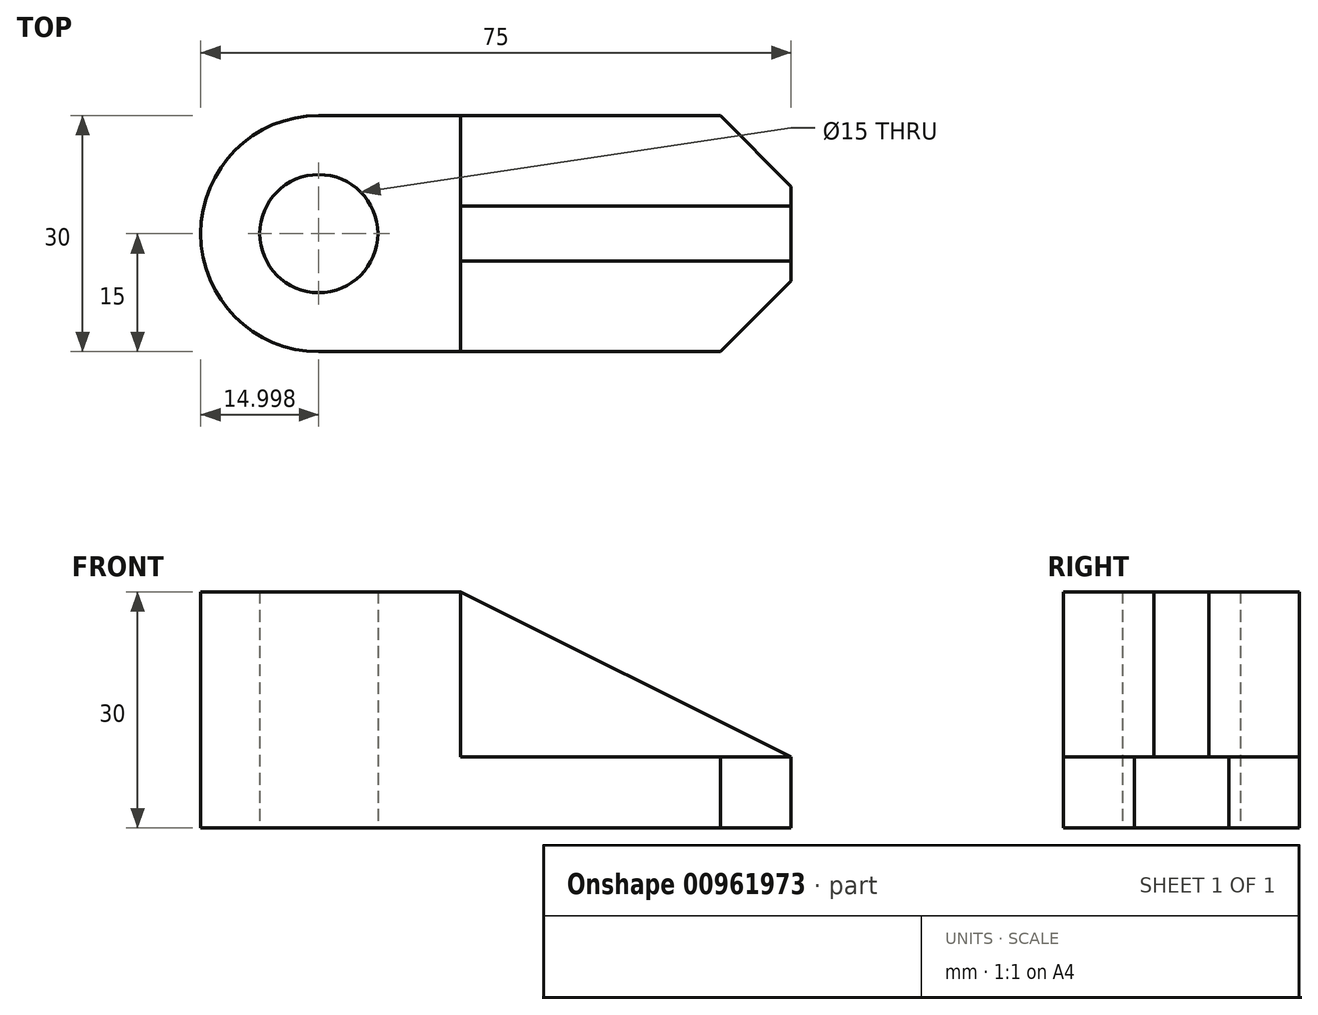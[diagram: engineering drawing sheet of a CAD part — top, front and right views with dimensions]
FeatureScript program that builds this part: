
annotation { "Feature Type Name" : "Feature", "Feature Type Description" : "" }
export const myFeature = defineFeature(function(context is Context, id is Id, definition is map)
    precondition{}
    {
        {
            var Q0;
            Q0=qCreatedBy(makeId("Top.planeOp"),FACE);
            var sketch = newSketch(context, id + "F0", { "sketchPlane" : qUnion([Q0])});
            skCircle(sketch, "E0", {"center": v(-60.56, 0) * mm, "radius": 7.5 * mm});
            skArc(sketch, "E1", {"start": v(-60.56, 15) * mm, "mid": v(-75.56, 0) * mm, "end": v(-60.56, -15) * mm});
            skLineSegment(sketch, "E2.bottom", {"start": v(-60.56, -15) * mm, "end": v(-0.56, -15) * mm});
            skLineSegment(sketch, "E2.top", {"start": v(-60.56, 15) * mm, "end": v(-0.56, 15) * mm});
            skLineSegment(sketch, "E2.right", {"start": v(-0.56, -15) * mm, "end": v(-0.56, 15) * mm});
            skLineSegment(sketch, "E3", {"start": v(-42.56, 15) * mm, "end": v(-42.56, -15) * mm});
            skSolve(sketch);
        }
        {
            var Q0;
            Q0=makeQuery(id+"F0.imprint","IMPRINT",FACE,{"disambiguationData":[TD([[makeQuery(id+"F0.imprint","IMPRINT",EDGE,{"derivedFrom":sQuery(id+"F0.wireOp",EDGE,"E0")}),-1.0]])]});
            extrude(context, id + "F1", {"entities" : qUnion([Q0]), "depth" : 30 * mm, "offsetDistance" : 25 * mm});
        }
        {
            var Q0;
            {var subQ0=sQuery(id+"F0.wireOp",EDGE,"E2.right");Q0=makeQuery(id+"F0.imprint","IMPRINT",FACE,{"disambiguationData":[TD([[makeQuery(id+"F0.imprint","IMPRINT",EDGE,{"derivedFrom":subQ0}),1.0]])]});}
            extrude(context, id + "F2", {"entities" : qUnion([Q0]), "operationType" : NewBodyOperationType.ADD, "depth" : 9 * mm, "offsetDistance" : 25 * mm});
        }
        {
            var Q0;
            Q0=makeQuery(id+"F2.opExtrude","SWEPT_EDGE",EDGE,{"disambiguationData":[OSD([sQuery(id+"F0.wireOp",EDGE,"E2.bottom"),sQuery(id+"F0.wireOp",EDGE,"E2.right")])]});
            var Q1;
            Q1=makeQuery(id+"F2.opExtrude","SWEPT_EDGE",EDGE,{"disambiguationData":[OSD([sQuery(id+"F0.wireOp",EDGE,"E2.top"),sQuery(id+"F0.wireOp",EDGE,"E2.right")])]});
            chamfer(context, id + "F3", {"entities" : qUnion([Q0, Q1]), "width" : 9 * mm, "tangentPropagation" : true});
        }
        {
            var Q0;
            Q0=qCreatedBy(makeId("Front.planeOp"),FACE);
            var sketch = newSketch(context, id + "F4", { "sketchPlane" : qUnion([Q0])});
            skPoint(sketch, "E4.0", {"position": v(-0.56, 9) * mm});
            skPoint(sketch, "E5.0", {"position": v(-42.56, 30) * mm});
            skLineSegment(sketch, "E6", {"start": v(-42.56, 30) * mm, "end": v(-0.56, 9) * mm});
            skLineSegment(sketch, "E7", {"start": v(-42.56, 9) * mm, "end": v(-42.56, 30) * mm});
            skLineSegment(sketch, "E8", {"start": v(-0.56, 9) * mm, "end": v(-42.56, 9) * mm});
            skSolve(sketch);
        }
        {
            var Q0;
            Q0=makeQuery(id+"F4.imprint","IMPRINT",FACE,{"disambiguationData":[TD([[makeQuery(id+"F4.imprint","IMPRINT",EDGE,{"derivedFrom":sQuery(id+"F4.wireOp",EDGE,"E6")}),-1.0]])]});
            extrude(context, id + "F5", {"entities" : qUnion([Q0]), "operationType" : NewBodyOperationType.ADD, "endBound" : BoundingType.SYMMETRIC, "depth" : 7 * mm, "offsetDistance" : 25 * mm});
        }
    });
